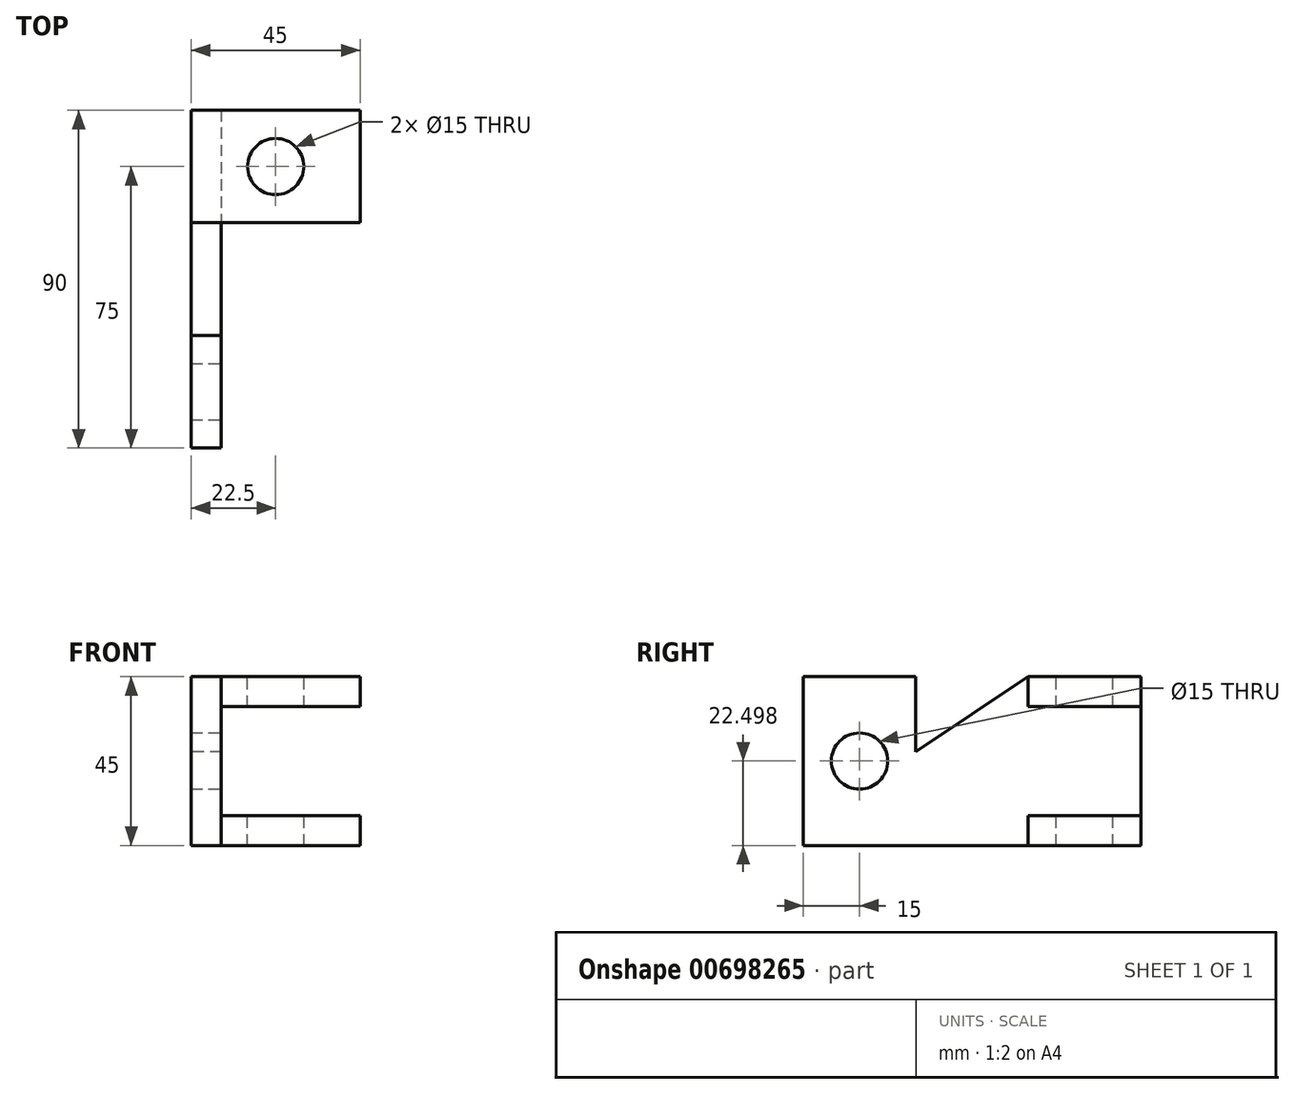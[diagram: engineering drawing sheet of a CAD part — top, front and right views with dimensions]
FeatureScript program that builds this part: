
annotation { "Feature Type Name" : "Feature", "Feature Type Description" : "" }
export const myFeature = defineFeature(function(context is Context, id is Id, definition is map)
    precondition{}
    {
        {
            var Q0;
            Q0=qCreatedBy(makeId("Right.planeOp"),FACE);
            var sketch = newSketch(context, id + "F0", { "sketchPlane" : qUnion([Q0])});
            skLineSegment(sketch, "E0", {"start": v(-60, 24.3) * mm, "end": v(-60, -20.7) * mm});
            skLineSegment(sketch, "E1", {"start": v(-60, -20.7) * mm, "end": v(30, -20.7) * mm});
            skLineSegment(sketch, "E2", {"start": v(30, -20.7) * mm, "end": v(30, 24.3) * mm});
            skLineSegment(sketch, "E3", {"start": v(30, 24.3) * mm, "end": v(0, 24.3) * mm});
            skLineSegment(sketch, "E4", {"start": v(0, 24.3) * mm, "end": v(-30, 4.3) * mm});
            skLineSegment(sketch, "E5", {"start": v(-30, 4.3) * mm, "end": v(-30, 24.3) * mm});
            skLineSegment(sketch, "E6", {"start": v(-30, 24.3) * mm, "end": v(-60, 24.3) * mm});
            skSolve(sketch);
        }
        {
            var Q0;
            Q0=makeQuery(id+"F0.imprint","IMPRINT",FACE,{"disambiguationData":[TD([[makeQuery(id+"F0.imprint","IMPRINT",EDGE,{"derivedFrom":sQuery(id+"F0.wireOp",EDGE,"E0")}),1.0]])]});
            extrude(context, id + "F1", {"entities" : qUnion([Q0]), "depth" : 8 * mm, "offsetDistance" : 25 * mm});
        }
        {
            var Q0;
            Q0=makeQuery(id+"F1.opExtrude","CAP_FACE",FACE,{"disambiguationData":[OSD([sQuery(id+"F0.wireOp",EDGE,"E0"),sQuery(id+"F0.wireOp",EDGE,"E1"),sQuery(id+"F0.wireOp",EDGE,"E2"),sQuery(id+"F0.wireOp",EDGE,"E3"),sQuery(id+"F0.wireOp",EDGE,"E4"),sQuery(id+"F0.wireOp",EDGE,"E5"),sQuery(id+"F0.wireOp",EDGE,"E6")])],"isStart":false});
            var sketch = newSketch(context, id + "F2", { "sketchPlane" : qUnion([Q0])});
            skLineSegment(sketch, "E7.bottom", {"start": v(0, 24.3) * mm, "end": v(30, 24.3) * mm});
            skLineSegment(sketch, "E7.top", {"start": v(0, 16.3) * mm, "end": v(30, 16.3) * mm});
            skLineSegment(sketch, "E7.left", {"start": v(0, 24.3) * mm, "end": v(0, 16.3) * mm});
            skLineSegment(sketch, "E7.right", {"start": v(30, 24.3) * mm, "end": v(30, 16.3) * mm});
            skLineSegment(sketch, "E8.bottom", {"start": v(30, -20.7) * mm, "end": v(0, -20.7) * mm});
            skLineSegment(sketch, "E8.top", {"start": v(30, -12.7) * mm, "end": v(0, -12.7) * mm});
            skLineSegment(sketch, "E8.left", {"start": v(30, -20.7) * mm, "end": v(30, -12.7) * mm});
            skLineSegment(sketch, "E8.right", {"start": v(0, -20.7) * mm, "end": v(0, -12.7) * mm});
            skSolve(sketch);
        }
        {
            var Q0;
            Q0=makeQuery(id+"F2.imprint","IMPRINT",FACE,{"disambiguationData":[TD([[makeQuery(id+"F2.imprint","IMPRINT",EDGE,{"derivedFrom":sQuery(id+"F2.wireOp",EDGE,"E8.bottom")}),1.0]])]});
            var Q1;
            Q1=makeQuery(id+"F2.imprint","IMPRINT",FACE,{"disambiguationData":[TD([[makeQuery(id+"F2.imprint","IMPRINT",EDGE,{"derivedFrom":sQuery(id+"F2.wireOp",EDGE,"E7.bottom")}),1.0]])]});
            extrude(context, id + "F3", {"entities" : qUnion([Q0, Q1]), "operationType" : NewBodyOperationType.ADD, "depth" : 37 * mm, "offsetDistance" : 25 * mm});
        }
        {
            var Q0;
            Q0=makeQuery(id+"F3.boolean.opBoolean","MERGE",FACE,{"derivedFrom":[makeQuery(id+"F1.opExtrude","SWEPT_FACE",FACE,{"disambiguationData":[OSD([sQuery(id+"F0.wireOp",EDGE,"E3")])]}),makeQuery(id+"F3.opExtrude","SWEPT_FACE",FACE,{"disambiguationData":[OSD([sQuery(id+"F2.wireOp",EDGE,"E7.bottom")])]})]});
            var sketch = newSketch(context, id + "F4", { "sketchPlane" : qUnion([Q0])});
            skLineSegment(sketch, "E9", {"start": v(45, 30) * mm, "end": v(22.5, 30) * mm});
            skLineSegment(sketch, "E10", {"start": v(22.5, 30) * mm, "end": v(22.5, 15) * mm});
            skPoint(sketch, "E10.endSnap0", {"position": v(45, 15) * mm});
            skSolve(sketch);
        }
        {
            var Q0;
            Q0=sQuery(id+"F4.wireOp",VERTEX,"E10.end");
            var Q1;
            Q1=makeQuery(id+"F1.opExtrude","SWEPT_BODY",BODY,{"disambiguationData":[OSD([sQuery(id+"F0.wireOp",EDGE,"E0"),sQuery(id+"F0.wireOp",EDGE,"E1"),sQuery(id+"F0.wireOp",EDGE,"E2"),sQuery(id+"F0.wireOp",EDGE,"E3"),sQuery(id+"F0.wireOp",EDGE,"E4"),sQuery(id+"F0.wireOp",EDGE,"E5"),sQuery(id+"F0.wireOp",EDGE,"E6")])]});
            hole(context, id + "F5", {"style" : HoleStyle.SIMPLE, "endStyle" : HoleEndStyle.THROUGH, "holeDiameter" : 15 * mm, "majorDiameter" : 5 * mm, "isTappedThrough" : true, "tappedDepth" : 12 * mm, "tapClearance" : 3, "locations" : qUnion([Q0]), "scope" : qUnion([Q1])});
        }
        {
            var Q0;
            Q0=makeQuery(id+"F1.opExtrude","CAP_FACE",FACE,{"disambiguationData":[OSD([sQuery(id+"F0.wireOp",EDGE,"E0"),sQuery(id+"F0.wireOp",EDGE,"E1"),sQuery(id+"F0.wireOp",EDGE,"E2"),sQuery(id+"F0.wireOp",EDGE,"E3"),sQuery(id+"F0.wireOp",EDGE,"E4"),sQuery(id+"F0.wireOp",EDGE,"E5"),sQuery(id+"F0.wireOp",EDGE,"E6")])],"isStart":false});
            var sketch = newSketch(context, id + "F6", { "sketchPlane" : qUnion([Q0])});
            skLineSegment(sketch, "E11", {"start": v(-60, 1.8) * mm, "end": v(-45, 1.8) * mm});
            skPoint(sketch, "E11.endSnap0", {"position": v(-45, 24.3) * mm});
            skSolve(sketch);
        }
        {
            var Q0;
            Q0=sQuery(id+"F6.wireOp",VERTEX,"E11.end");
            var Q1;
            Q1=makeQuery(id+"F1.opExtrude","SWEPT_BODY",BODY,{"disambiguationData":[OSD([sQuery(id+"F0.wireOp",EDGE,"E0"),sQuery(id+"F0.wireOp",EDGE,"E1"),sQuery(id+"F0.wireOp",EDGE,"E2"),sQuery(id+"F0.wireOp",EDGE,"E3"),sQuery(id+"F0.wireOp",EDGE,"E4"),sQuery(id+"F0.wireOp",EDGE,"E5"),sQuery(id+"F0.wireOp",EDGE,"E6")])]});
            hole(context, id + "F7", {"style" : HoleStyle.SIMPLE, "endStyle" : HoleEndStyle.THROUGH, "holeDiameter" : 15 * mm, "majorDiameter" : 5 * mm, "isTappedThrough" : true, "tappedDepth" : 12 * mm, "tapClearance" : 3, "locations" : qUnion([Q0]), "scope" : qUnion([Q1])});
        }
    });
